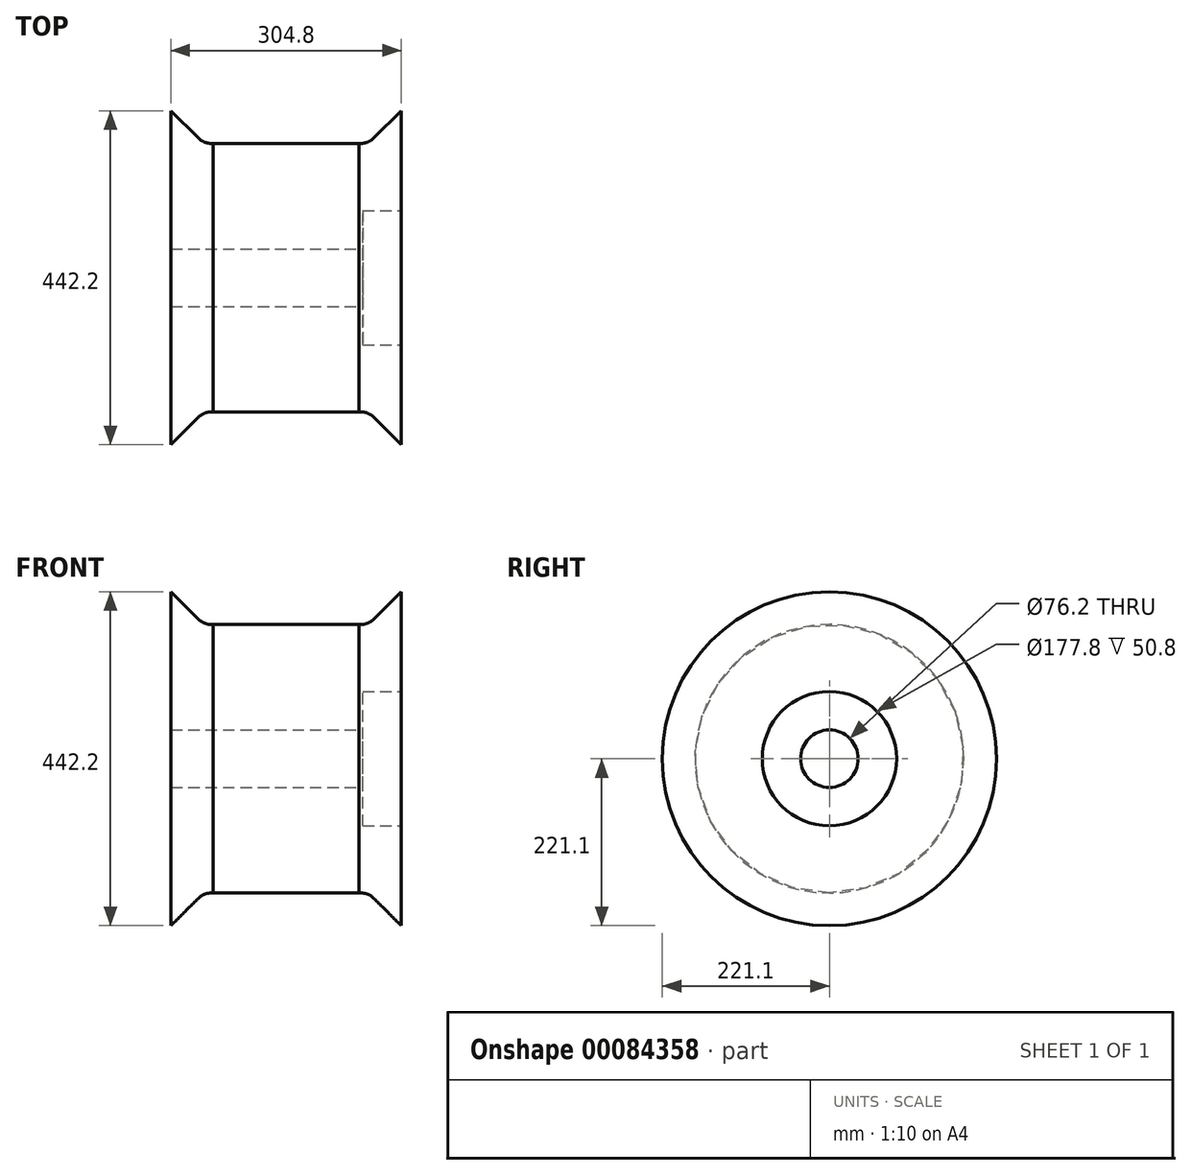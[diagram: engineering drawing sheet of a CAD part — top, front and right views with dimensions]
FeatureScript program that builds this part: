
annotation { "Feature Type Name" : "Feature", "Feature Type Description" : "" }
export const myFeature = defineFeature(function(context is Context, id is Id, definition is map)
    precondition{}
    {
        {
            var Q0;
            Q0=qCreatedBy(makeId("Front.planeOp"),FACE);
            var sketch = newSketch(context, id + "F0", { "sketchPlane" : qUnion([Q0])});
            skLineSegment(sketch, "E0", {"start": v(0, 0) * mm, "end": v(0, 152.4) * mm});
            skLineSegment(sketch, "E1", {"start": v(0, 152.4) * mm, "end": v(-96.76, 152.4) * mm});
            skLineSegment(sketch, "E2", {"start": v(0, 0) * mm, "end": v(-152.4, 0) * mm});
            skLineSegment(sketch, "E3", {"start": v(-152.4, 0) * mm, "end": v(-152.4, 195.7) * mm});
            skLineSegment(sketch, "E4", {"start": v(-152.4, 195.7) * mm, "end": v(-116.48, 159.78) * mm});
            skArc(sketch, "E5", {"start": v(-116.48, 159.78) * mm, "mid": v(-107.42, 153.95) * mm, "end": v(-96.76, 152.4) * mm});
            skLineSegment(sketch, "E6", {"start": v(0, -25.4) * mm, "end": v(-255.95, -25.4) * mm, "construction": true});
            skSolve(sketch);
        }
        {
            var Q0;
            Q0 = qSketchRegion(id + "F0", true);
            var Q1;
            Q1=sQuery(id+"F0.wireOp",EDGE,"E6");
            revolve(context, id + "F1", {"entities" : qUnion([Q0]), "axis" : qUnion([Q1]), "revolveType" : RevolveType.FULL});
        }
        {
            var Q0;
            Q0=makeQuery(id+"F1.opRevolve","SWEPT_BODY",BODY,{"disambiguationData":[OSD([sQuery(id+"F0.wireOp",EDGE,"E0"),sQuery(id+"F0.wireOp",EDGE,"E1"),sQuery(id+"F0.wireOp",EDGE,"E2"),sQuery(id+"F0.wireOp",EDGE,"E3"),sQuery(id+"F0.wireOp",EDGE,"E4"),sQuery(id+"F0.wireOp",EDGE,"E5")])]});
            var Q1;
            Q1=makeQuery(id+"F1.opRevolve","SWEPT_FACE",FACE,{"disambiguationData":[OSD([sQuery(id+"F0.wireOp",EDGE,"E0")])]});
            mirror(context, id + "F2", {"operationType" : NewBodyOperationType.ADD, "entities" : qUnion([Q0]), "mirrorPlane" : qUnion([Q1])});
        }
        {
            var Q0;
            Q0=makeQuery(id+"F2.opPattern","COPY",FACE,{"derivedFrom":makeQuery(id+"F1.opRevolve","SWEPT_FACE",FACE,{"disambiguationData":[OSD([sQuery(id+"F0.wireOp",EDGE,"E3")])]}),"instanceName":"1"});
            var sketch = newSketch(context, id + "F3", { "sketchPlane" : qUnion([Q0])});
            skCircle(sketch, "E7.0", {"center": v(0, -25.4) * mm, "radius": 221.1 * mm});
            skCircle(sketch, "E8", {"center": v(0, -25.4) * mm, "radius": 38.1 * mm});
            skSolve(sketch);
        }
        {
            var Q0;
            Q0=makeQuery(id+"F3.imprint","IMPRINT",FACE,{"disambiguationData":[TD([[makeQuery(id+"F3.imprint","IMPRINT",EDGE,{"derivedFrom":sQuery(id+"F3.wireOp",EDGE,"E8")}),1.0]])]});
            extrude(context, id + "F4", {"entities" : qUnion([Q0]), "operationType" : NewBodyOperationType.REMOVE, "endBound" : BoundingType.THROUGH_ALL, "oppositeDirection" : true, "depth" : 25.4 * mm});
        }
        {
            var Q0;
            Q0=makeQuery(id+"F2.opPattern","COPY",FACE,{"derivedFrom":makeQuery(id+"F1.opRevolve","SWEPT_FACE",FACE,{"disambiguationData":[OSD([sQuery(id+"F0.wireOp",EDGE,"E3")])]}),"instanceName":"1"});
            var sketch = newSketch(context, id + "F5", { "sketchPlane" : qUnion([Q0])});
            skCircle(sketch, "E9.0", {"center": v(0, -25.4) * mm, "radius": 221.1 * mm});
            skCircle(sketch, "E10.0", {"center": v(0, -25.4) * mm, "radius": 88.9 * mm});
            skSolve(sketch);
        }
        {
            var Q0;
            Q0=makeQuery(id+"F5.imprint","IMPRINT",FACE,{"disambiguationData":[TD([[makeQuery(id+"F5.imprint","IMPRINT",EDGE,{"derivedFrom":sQuery(id+"F5.wireOp",EDGE,"E10.0")}),1.0]])]});
            extrude(context, id + "F6", {"entities" : qUnion([Q0]), "operationType" : NewBodyOperationType.REMOVE, "oppositeDirection" : true, "depth" : 50.8 * mm});
        }
    });
